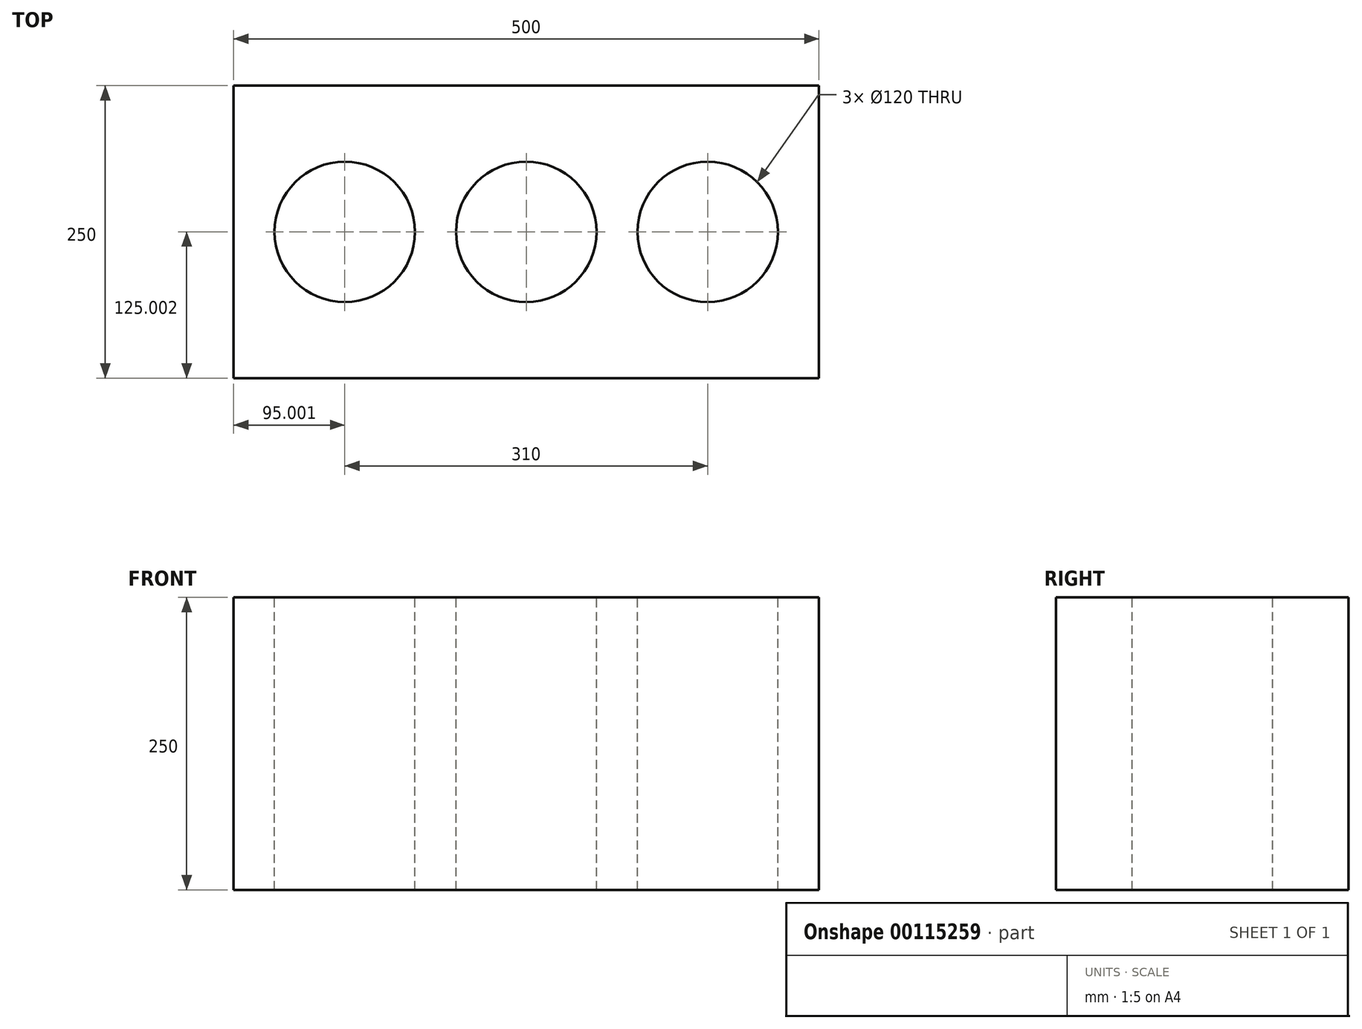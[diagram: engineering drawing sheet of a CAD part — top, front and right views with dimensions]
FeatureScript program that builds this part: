
annotation { "Feature Type Name" : "Feature", "Feature Type Description" : "" }
export const myFeature = defineFeature(function(context is Context, id is Id, definition is map)
    precondition{}
    {
        {
            var Q0;
            Q0=qCreatedBy(makeId("Top.planeOp"),FACE);
            var sketch = newSketch(context, id + "F0", { "sketchPlane" : qUnion([Q0])});
            skLineSegment(sketch, "E0.bottom", {"start": v(-52.3, 183.78) * mm, "end": v(447.7, 183.78) * mm});
            skLineSegment(sketch, "E0.top", {"start": v(-52.3, -66.22) * mm, "end": v(447.7, -66.22) * mm});
            skLineSegment(sketch, "E0.left", {"start": v(-52.3, 183.78) * mm, "end": v(-52.3, -66.22) * mm});
            skLineSegment(sketch, "E0.right", {"start": v(447.7, 183.78) * mm, "end": v(447.7, -66.22) * mm});
            skSolve(sketch);
        }
        {
            var Q0;
            Q0=makeQuery(id+"F0.imprint","IMPRINT",FACE,{"disambiguationData":[TD([[makeQuery(id+"F0.imprint","IMPRINT",EDGE,{"derivedFrom":sQuery(id+"F0.wireOp",EDGE,"E0.bottom")}),-1.0]])]});
            extrude(context, id + "F1", {"entities" : qUnion([Q0]), "depth" : 250 * mm});
        }
        {
            var Q0;
            Q0=makeQuery(id+"F1.opExtrude","CAP_FACE",FACE,{"disambiguationData":[OSD([sQuery(id+"F0.wireOp",EDGE,"E0.bottom"),sQuery(id+"F0.wireOp",EDGE,"E0.top"),sQuery(id+"F0.wireOp",EDGE,"E0.left"),sQuery(id+"F0.wireOp",EDGE,"E0.right")])],"isStart":false});
            var sketch = newSketch(context, id + "F2", { "sketchPlane" : qUnion([Q0])});
            skCircle(sketch, "E1", {"center": v(42.7, 58.78) * mm, "radius": 60 * mm});
            skCircle(sketch, "E2", {"center": v(197.7, 58.78) * mm, "radius": 60 * mm});
            skCircle(sketch, "E3", {"center": v(352.7, 58.78) * mm, "radius": 60 * mm});
            skSolve(sketch);
        }
        {
            var Q0;
            Q0=makeQuery(id+"F2.imprint","IMPRINT",FACE,{"disambiguationData":[TD([[makeQuery(id+"F2.imprint","IMPRINT",EDGE,{"derivedFrom":sQuery(id+"F2.wireOp",EDGE,"E1")}),1.0]])]});
            var Q1;
            Q1=makeQuery(id+"F2.imprint","IMPRINT",FACE,{"disambiguationData":[TD([[makeQuery(id+"F2.imprint","IMPRINT",EDGE,{"derivedFrom":sQuery(id+"F2.wireOp",EDGE,"E2")}),1.0]])]});
            var Q2;
            Q2=makeQuery(id+"F2.imprint","IMPRINT",FACE,{"disambiguationData":[TD([[makeQuery(id+"F2.imprint","IMPRINT",EDGE,{"derivedFrom":sQuery(id+"F2.wireOp",EDGE,"E3")}),1.0]])]});
            extrude(context, id + "F3", {"entities" : qUnion([Q0, Q1, Q2]), "operationType" : NewBodyOperationType.REMOVE, "oppositeDirection" : true, "depth" : 250 * mm});
        }
    });
